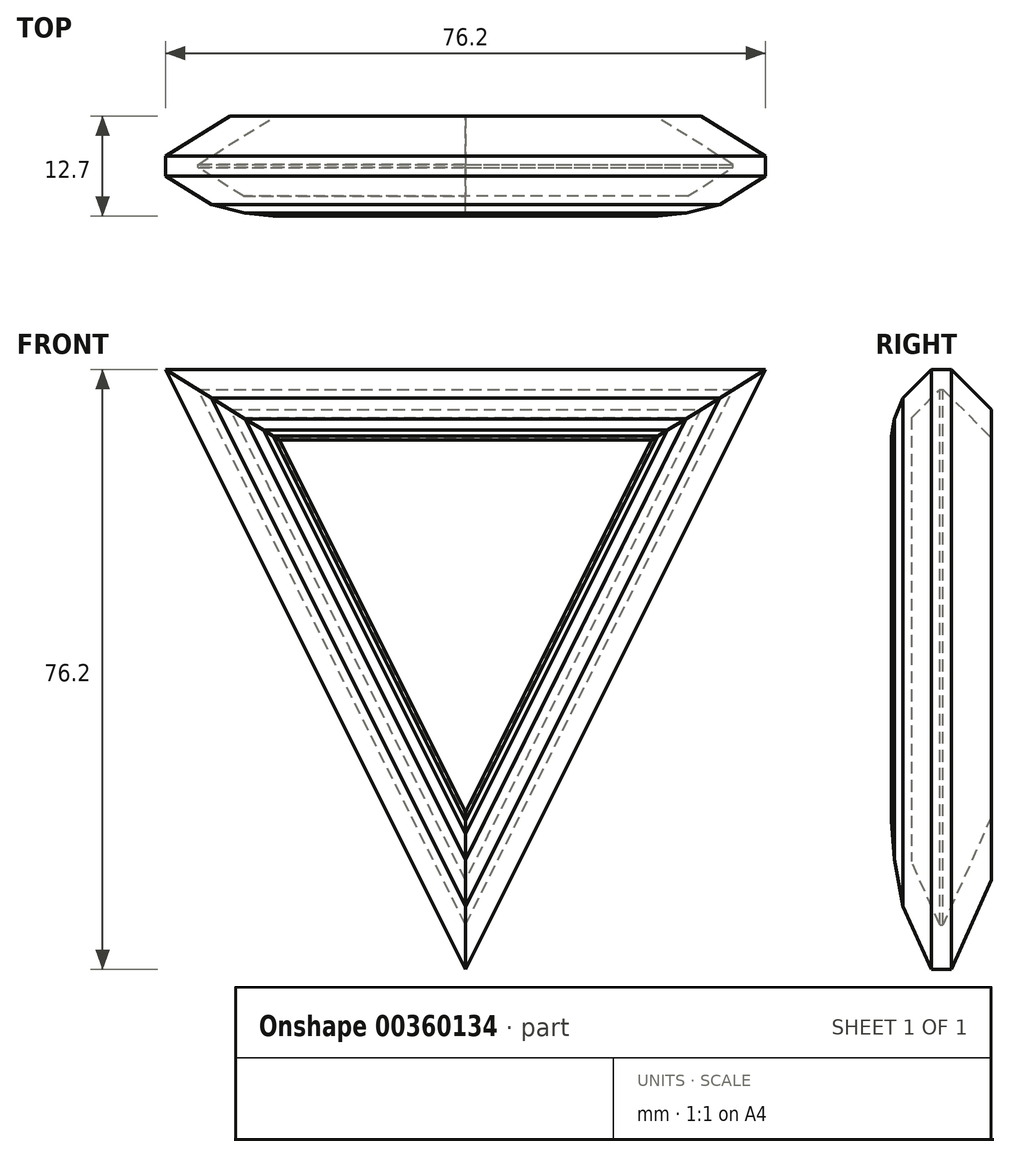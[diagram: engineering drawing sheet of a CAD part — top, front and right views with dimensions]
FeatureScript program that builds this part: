
annotation { "Feature Type Name" : "Feature", "Feature Type Description" : "" }
export const myFeature = defineFeature(function(context is Context, id is Id, definition is map)
    precondition{}
    {
        {
            var Q0;
            Q0=qCreatedBy(makeId("Front.planeOp"),FACE);
            var sketch = newSketch(context, id + "F0", { "sketchPlane" : qUnion([Q0])});
            skLineSegment(sketch, "E0", {"start": v(-38.1, 38.1) * mm, "end": v(0, -38.1) * mm});
            skLineSegment(sketch, "E1", {"start": v(38.1, 38.1) * mm, "end": v(0, -38.1) * mm});
            skLineSegment(sketch, "E2", {"start": v(38.1, 38.1) * mm, "end": v(-38.1, 38.1) * mm});
            skLineSegment(sketch, "E3", {"start": v(0, 0) * mm, "end": v(38.1, 38.1) * mm});
            skLineSegment(sketch, "E4", {"start": v(0, 0) * mm, "end": v(-38.1, 38.1) * mm});
            skLineSegment(sketch, "E5", {"start": v(0, 0) * mm, "end": v(0, -38.1) * mm});
            skSolve(sketch);
        }
        {
            var Q0;
            Q0 = qSketchRegion(id + "F0", true);
            extrude(context, id + "F1", {"entities" : qUnion([Q0]), "depth" : 12.7 * mm});
        }
        {
            var Q0;
            Q0=makeQuery(id+"F1.opExtrude","CAP_EDGE",EDGE,{"disambiguationData":[OSD([sQuery(id+"F0.wireOp",EDGE,"E2")])],"isStart":false});
            var Q1;
            Q1=makeQuery(id+"F1.opExtrude","CAP_EDGE",EDGE,{"disambiguationData":[OSD([sQuery(id+"F0.wireOp",EDGE,"E0")])],"isStart":false});
            var Q2;
            Q2=makeQuery(id+"F1.opExtrude","CAP_EDGE",EDGE,{"disambiguationData":[OSD([sQuery(id+"F0.wireOp",EDGE,"E1")])],"isStart":false});
            var Q3;
            Q3=makeQuery(id+"F1.opExtrude","CAP_EDGE",EDGE,{"disambiguationData":[OSD([sQuery(id+"F0.wireOp",EDGE,"E0")])],"isStart":true});
            var Q4;
            Q4=makeQuery(id+"F1.opExtrude","CAP_EDGE",EDGE,{"disambiguationData":[OSD([sQuery(id+"F0.wireOp",EDGE,"E2")])],"isStart":true});
            var Q5;
            Q5=makeQuery(id+"F1.opExtrude","CAP_EDGE",EDGE,{"disambiguationData":[OSD([sQuery(id+"F0.wireOp",EDGE,"E1")])],"isStart":true});
            chamfer(context, id + "F2", {"entities" : qUnion([Q0, Q1, Q2, Q3, Q4, Q5]), "width" : 5.08 * mm, "tangentPropagation" : true});
        }
        {
            var Q0;
            Q0=makeQuery(id+"F1.opExtrude","CAP_FACE",FACE,{"disambiguationData":[OSD([sQuery(id+"F0.wireOp",EDGE,"E0"),sQuery(id+"F0.wireOp",EDGE,"E1"),sQuery(id+"F0.wireOp",EDGE,"E2")])],"isStart":true});
            shell(context, id + "F3", {"entities" : qUnion([Q0]), "thickness" : 2.54 * mm});
        }
        {
            var Q0;
            Q0=makeQuery(id+"F1.opExtrude","CAP_FACE",FACE,{"disambiguationData":[OSD([sQuery(id+"F0.wireOp",EDGE,"E0"),sQuery(id+"F0.wireOp",EDGE,"E1"),sQuery(id+"F0.wireOp",EDGE,"E2")])],"isStart":false});
            chamfer(context, id + "F4", {"entities" : qUnion([Q0]), "width" : 5.08 * mm, "tangentPropagation" : true});
        }
        {
            var Q0;
            Q0=makeQuery(id+"F1.opExtrude","CAP_FACE",FACE,{"disambiguationData":[OSD([sQuery(id+"F0.wireOp",EDGE,"E0"),sQuery(id+"F0.wireOp",EDGE,"E1"),sQuery(id+"F0.wireOp",EDGE,"E2")])],"isStart":false});
            chamfer(context, id + "F5", {"entities" : qUnion([Q0]), "width" : 5.08 * mm, "tangentPropagation" : true});
        }
        {
            var Q0;
            Q0=makeQuery(id+"F1.opExtrude","CAP_FACE",FACE,{"disambiguationData":[OSD([sQuery(id+"F0.wireOp",EDGE,"E0"),sQuery(id+"F0.wireOp",EDGE,"E1"),sQuery(id+"F0.wireOp",EDGE,"E2")])],"isStart":false});
            chamfer(context, id + "F6", {"entities" : qUnion([Q0]), "width" : 5.08 * mm, "tangentPropagation" : true});
        }
        {
            var Q0;
            Q0=makeQuery(id+"F1.opExtrude","CAP_FACE",FACE,{"disambiguationData":[OSD([sQuery(id+"F0.wireOp",EDGE,"E0"),sQuery(id+"F0.wireOp",EDGE,"E1"),sQuery(id+"F0.wireOp",EDGE,"E2")])],"isStart":false});
            chamfer(context, id + "F7", {"entities" : qUnion([Q0]), "width" : 5.08 * mm, "tangentPropagation" : true});
        }
    });
